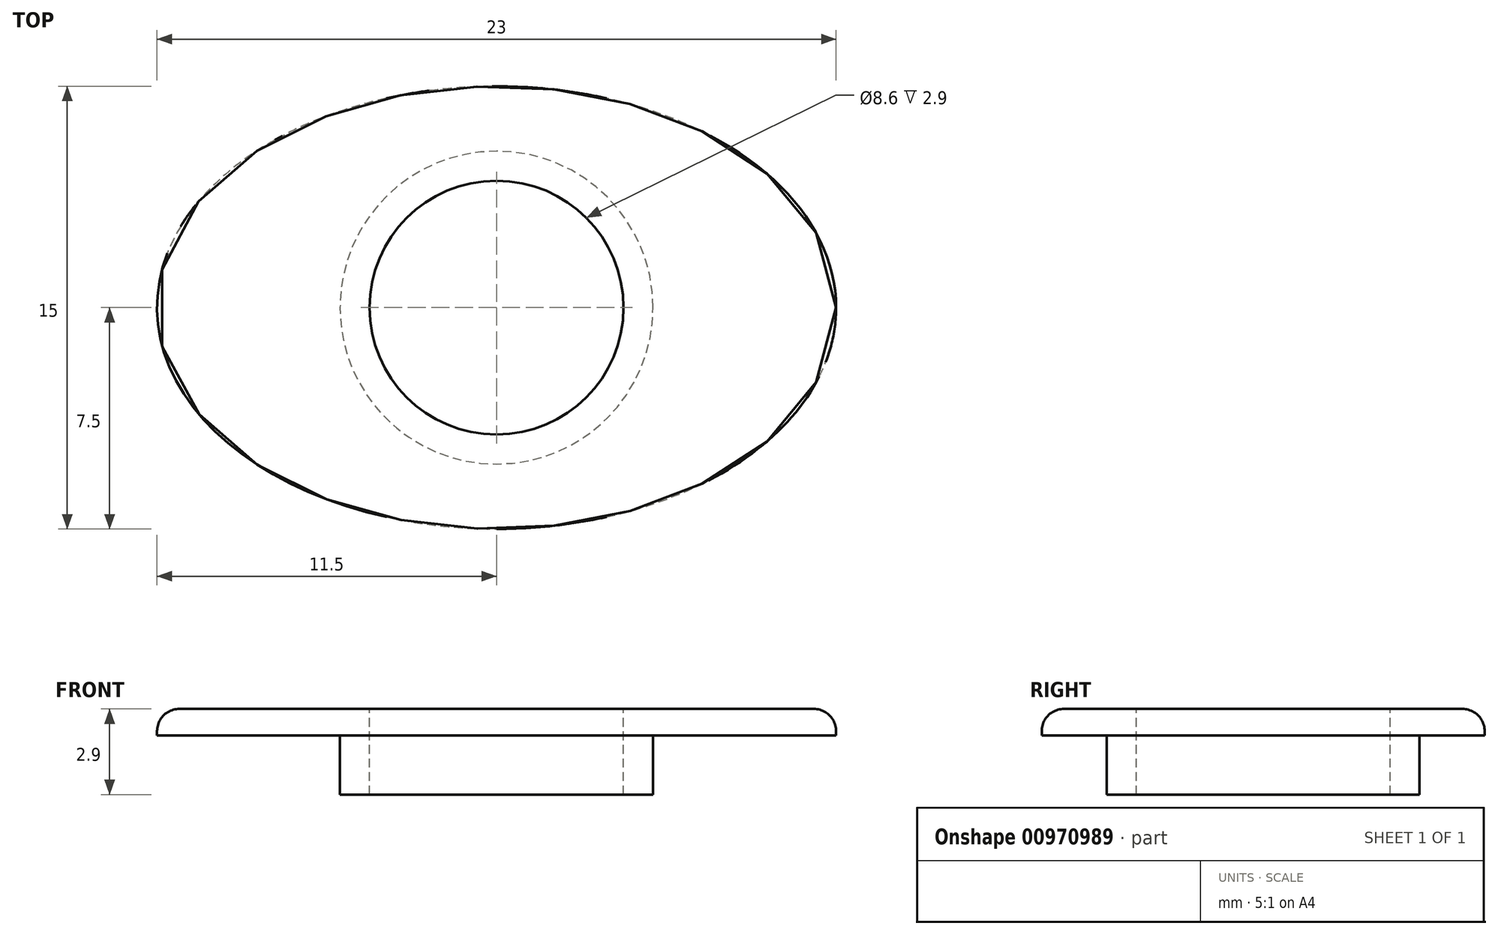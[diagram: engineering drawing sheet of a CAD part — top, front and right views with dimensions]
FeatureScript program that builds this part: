
annotation { "Feature Type Name" : "Feature", "Feature Type Description" : "" }
export const myFeature = defineFeature(function(context is Context, id is Id, definition is map)
    precondition{}
    {
        {
            var Q0;
            Q0=qCreatedBy(makeId("Top.planeOp"),FACE);
            var sketch = newSketch(context, id + "F0", { "sketchPlane" : qUnion([Q0])});
            skPoint(sketch, "E0.middle", {"position": v(0, 0) * mm});
            skCircle(sketch, "E1", {"center": v(0, 0) * mm, "radius": 4.3 * mm});
            skEllipse(sketch, "E2", {"center": v(0, 0) * mm, "majorRadius": 11.5 * mm, "minorRadius": 7.5 * mm, "majorAxis": v(1, 0)});
            skSolve(sketch);
        }
        {
            var Q0;
            Q0=makeQuery(id+"F0.imprint","IMPRINT",FACE,{"disambiguationData":[TD([[makeQuery(id+"F0.imprint","IMPRINT",EDGE,{"derivedFrom":sQuery(id+"F0.wireOp",EDGE,"E0.bottom")}),1.0]])]});
            var Q1;
            Q1=makeQuery(id+"F0.imprint","IMPRINT",FACE,{"disambiguationData":[TD([[makeQuery(id+"F0.imprint","IMPRINT",EDGE,{"derivedFrom":sQuery(id+"F0.wireOp",EDGE,"KCpl4Vy5-C4OL-JF8E-t3t9-8lsWkRrDdORL")}),-1.0]])]});
            var Q2;
            Q2=makeQuery(id+"F0.imprint","IMPRINT",FACE,{"disambiguationData":[TD([[makeQuery(id+"F0.imprint","IMPRINT",EDGE,{"derivedFrom":sQuery(id+"F0.wireOp",EDGE,"E1")}),-1.0]])]});
            extrude(context, id + "F1", {"entities" : qUnion([Q0, Q1, Q2]), "oppositeDirection" : true, "depth" : 2.9 * mm, "offsetDistance" : 25 * mm});
        }
        {
            var Q0;
            Q0=makeQuery(id+"F1.opExtrude","CAP_FACE",FACE,{"disambiguationData":[OSD([sQuery(id+"F0.wireOp",EDGE,"E1"),sQuery(id+"F0.wireOp",EDGE,"E2")])],"isStart":false});
            var sketch = newSketch(context, id + "F2", { "sketchPlane" : qUnion([Q0])});
            skEllipse(sketch, "E3.0", {"center": v(0, 0) * mm, "majorRadius": 11.5 * mm, "minorRadius": 7.5 * mm, "majorAxis": v(1, 0)});
            skCircle(sketch, "E4.0", {"center": v(0, 0) * mm, "radius": 4.3 * mm, "construction": true});
            skCircle(sketch, "E5", {"center": v(0, 0) * mm, "radius": 5.3 * mm});
            skSolve(sketch);
        }
        {
            var Q0;
            Q0 = qSketchRegion(id + "F2", true);
            extrude(context, id + "F3", {"entities" : qUnion([Q0]), "operationType" : NewBodyOperationType.REMOVE, "oppositeDirection" : true, "depth" : 2 * mm, "offsetDistance" : 25 * mm});
        }
        {
            var Q0;
            Q0=makeQuery(id+"F1.opExtrude","CAP_EDGE",EDGE,{"disambiguationData":[OSD([sQuery(id+"F0.wireOp",EDGE,"E2")])],"isStart":true});
            var Q1;
            Q1=makeQuery(id+"F3.boolean.opBoolean","COPY",EDGE,{"derivedFrom":makeQuery(id+"F3.opExtrude","CAP_EDGE",EDGE,{"disambiguationData":[OSD([sQuery(id+"F2.wireOp",EDGE,"E5")])],"isStart":true})});
            fillet(context, id + "F4", {"entities" : qUnion([Q0, Q1]), "radius" : 0.75 * mm, "tangentPropagation" : true, "allowEdgeOverflow" : false});
        }
    });
